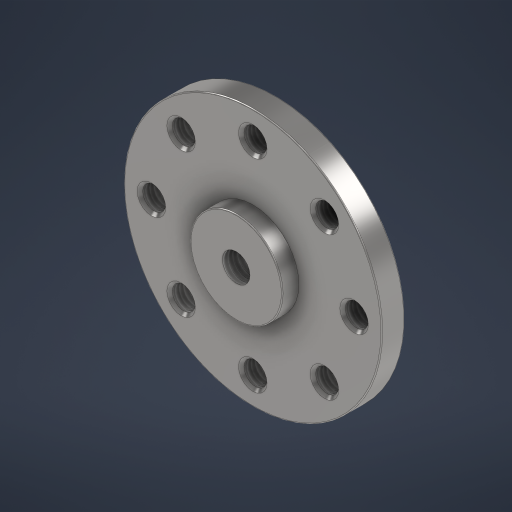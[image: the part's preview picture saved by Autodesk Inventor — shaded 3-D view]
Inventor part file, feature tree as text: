
AUTODESK INVENTOR PART (.ipt)
format: ipt  version: 2024 (Build 280153000, 153)  size: 299,520 bytes
history: native  units: mm
features: other x15, sketch x3, extrude x3, fillet x2, reference x2, chamfer x1, projected_geometry x1
ambient origin geometry x8: Origin, YZ Plane, XZ Plane, XY Plane, X Axis, Y Axis, Z Axis, Center Point
bodies: Body1 (feature_tree)
feature tree (27):
  other  "솔리드1"
  other  "작업 평면1"
  sketch  "스케치1"
  other  "작업 평면2"
  extrude  "돌출1"  Depth=10.0mm TaperAngle=0.0deg
  sketch  "스케치2"
  other  "작업 평면3"
  extrude  "돌출2"  Depth=3.0mm
  extrude  "돌출3"  Depth=10.0mm TaperAngle=0.0deg
  other  "스레드1"
  fillet  "모깎기1"  [1 undecoded]
  fillet  "모깎기2"  Radius=4.3mm
  other  "스레드2"
  other  "스레드3"
  other  "스레드4"
  other  "스레드5"
  other  "스레드6"
  other  "스레드7"
  other  "스레드8"
  other  "스레드9"
  chamfer  "모따기1"  Distance=0.1mm
  reference  "참조1"
  reference  "참조2"
  sketch  "스케치3"
  projected_geometry  "투영된 루프1"
  other  "Roll_Fixation_Set.iam"
  other  "MX-64T:2"
note: 1 required parameter value undecoded (feature->parameter linkage not recoverable at this tier; creation-order binding heuristic only, values carry confidence <= 0.55)
